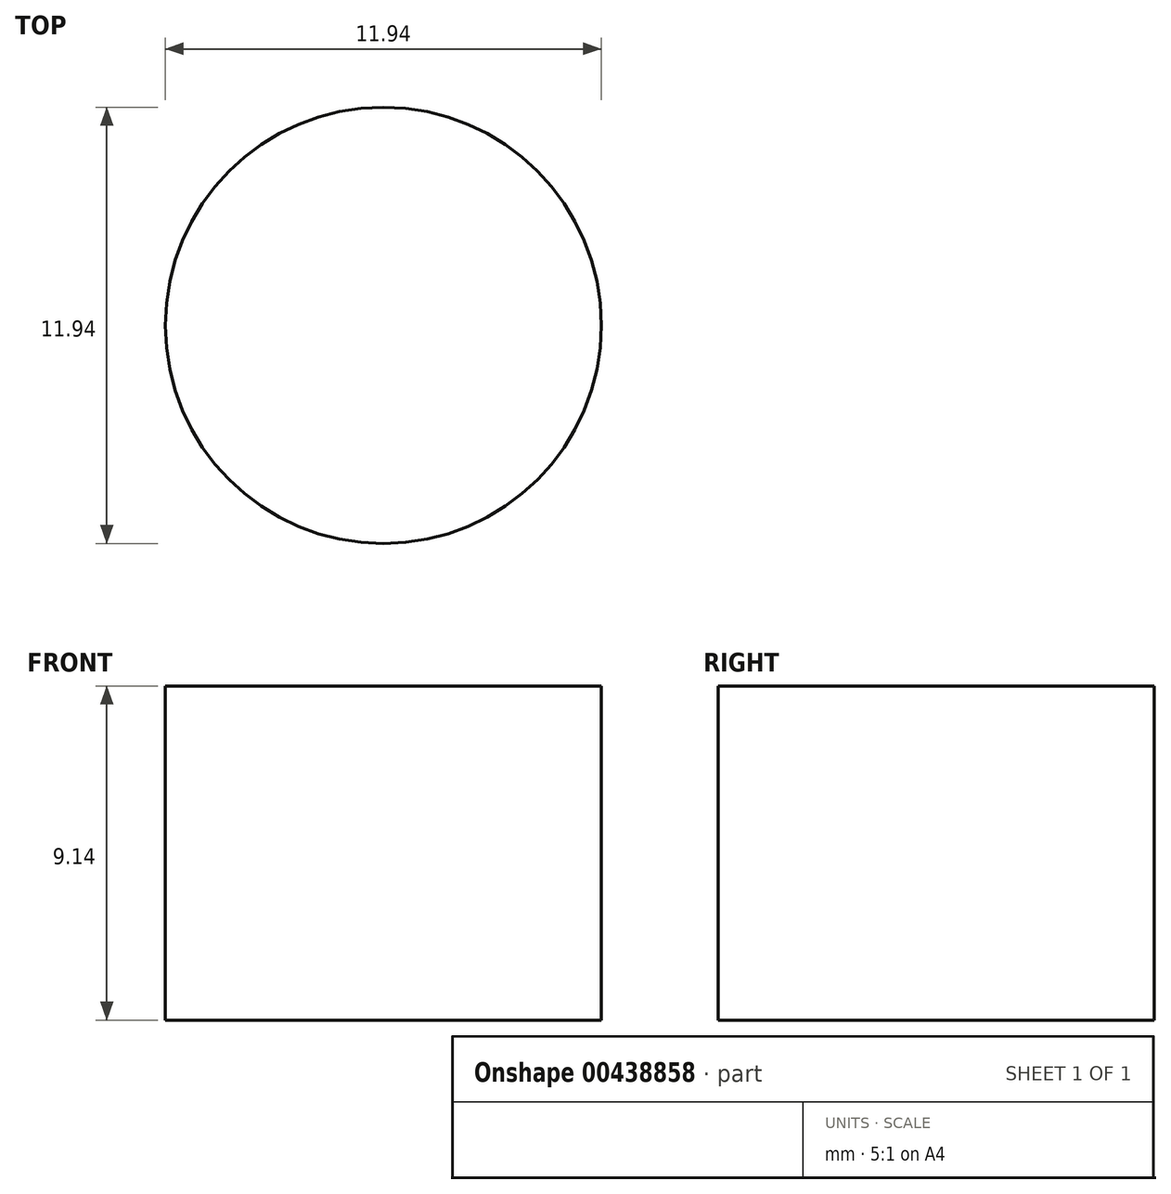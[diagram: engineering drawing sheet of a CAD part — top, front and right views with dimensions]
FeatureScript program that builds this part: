
annotation { "Feature Type Name" : "Feature", "Feature Type Description" : "" }
export const myFeature = defineFeature(function(context is Context, id is Id, definition is map)
    precondition{}
    {
        {
            var Q0;
            Q0=qCreatedBy(makeId("Top.planeOp"),FACE);
            var sketch = newSketch(context, id + "F0", { "sketchPlane" : qUnion([Q0])});
            skCircle(sketch, "E0", {"center": v(0, 0) * mm, "radius": 5.97 * mm});
            skSolve(sketch);
        }
        {
            var Q0;
            Q0 = qSketchRegion(id + "F0", true);
            extrude(context, id + "F1", {"entities" : qUnion([Q0]), "depth" : 9.14 * mm, "offsetDistance" : 25.4 * mm});
        }
    });
